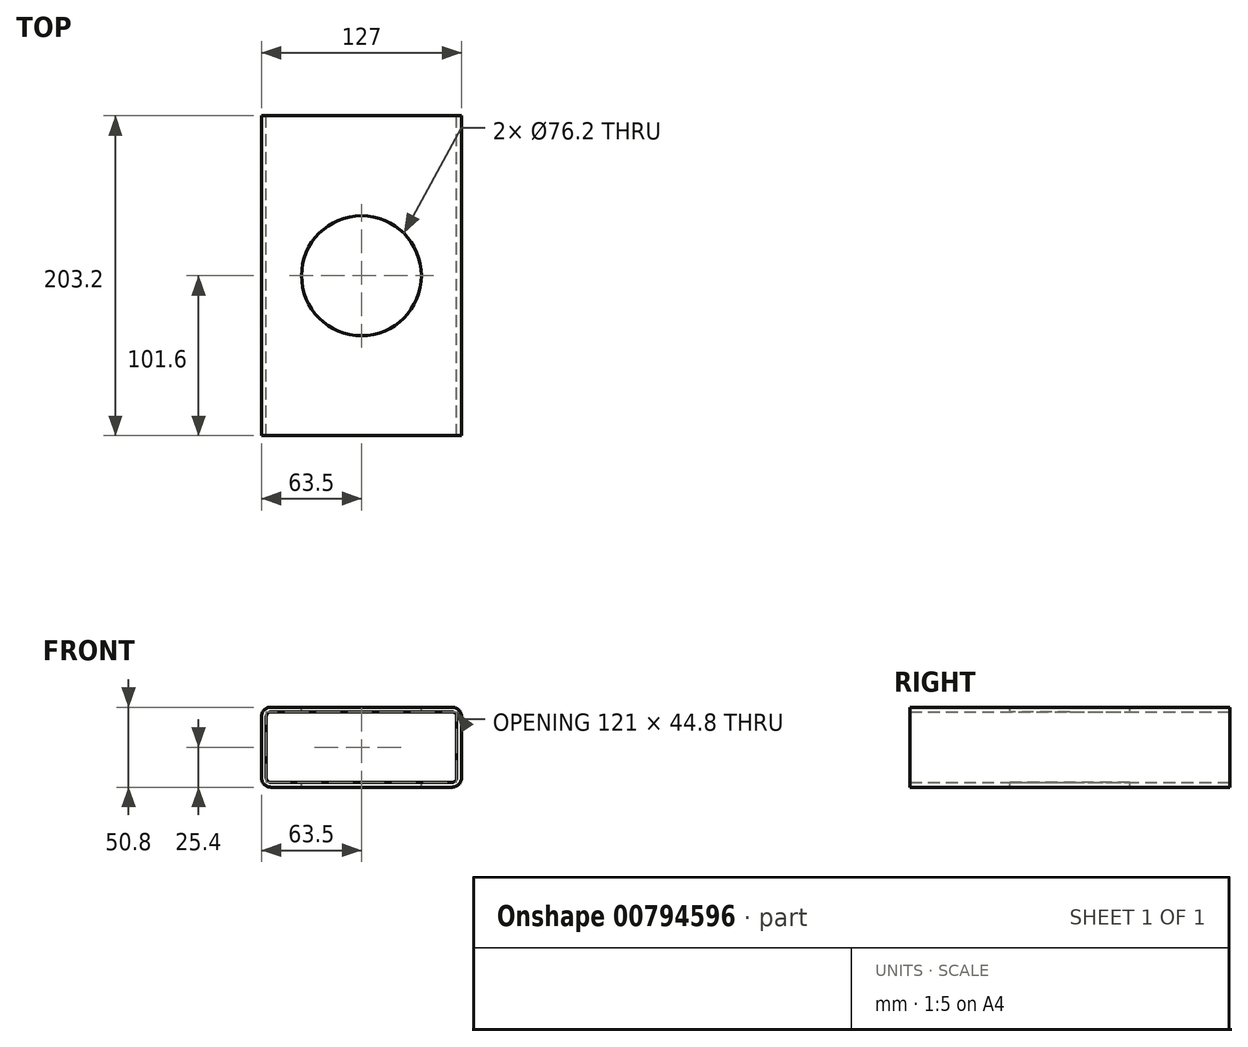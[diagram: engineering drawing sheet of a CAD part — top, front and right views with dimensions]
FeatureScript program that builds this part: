
annotation { "Feature Type Name" : "Feature", "Feature Type Description" : "" }
export const myFeature = defineFeature(function(context is Context, id is Id, definition is map)
    precondition{}
    {
        {
            var Q0;
            Q0=qCreatedBy(makeId("Front.planeOp"),FACE);
            var sketch = newSketch(context, id + "F0", { "sketchPlane" : qUnion([Q0])});
            skLineSegment(sketch, "E0.bottom", {"start": v(57.5, -25.4) * mm, "end": v(-57.5, -25.4) * mm});
            skLineSegment(sketch, "E0.top", {"start": v(57.5, 25.4) * mm, "end": v(-57.5, 25.4) * mm});
            skLineSegment(sketch, "E0.left", {"start": v(63.5, -19.4) * mm, "end": v(63.5, 19.4) * mm});
            skLineSegment(sketch, "E0.right", {"start": v(-63.5, -19.4) * mm, "end": v(-63.5, 19.4) * mm});
            skPoint(sketch, "E0.middle", {"position": v(0, 0) * mm});
            skLineSegment(sketch, "E1.bottom", {"start": v(57.5, -22.4) * mm, "end": v(-57.5, -22.4) * mm});
            skLineSegment(sketch, "E1.top", {"start": v(57.5, 22.4) * mm, "end": v(-57.5, 22.4) * mm});
            skLineSegment(sketch, "E1.left", {"start": v(60.5, -19.4) * mm, "end": v(60.5, 19.4) * mm});
            skLineSegment(sketch, "E1.right", {"start": v(-60.5, -19.4) * mm, "end": v(-60.5, 19.4) * mm});
            skPoint(sketch, "E2.visualSharp", {"position": v(-60.5, 22.4) * mm});
            skArc(sketch, "E2.filletArc", {"start": v(-57.5, 22.4) * mm, "mid": v(-59.62, 21.52) * mm, "end": v(-60.5, 19.4) * mm});
            skPoint(sketch, "E3.visualSharp", {"position": v(-60.5, -22.4) * mm});
            skArc(sketch, "E3.filletArc", {"start": v(-60.5, -19.4) * mm, "mid": v(-59.62, -21.52) * mm, "end": v(-57.5, -22.4) * mm});
            skPoint(sketch, "E4.visualSharp", {"position": v(60.5, -22.4) * mm});
            skArc(sketch, "E4.filletArc", {"start": v(57.5, -22.4) * mm, "mid": v(59.62, -21.52) * mm, "end": v(60.5, -19.4) * mm});
            skPoint(sketch, "E5.visualSharp", {"position": v(60.5, 22.4) * mm});
            skArc(sketch, "E5.filletArc", {"start": v(60.5, 19.4) * mm, "mid": v(59.62, 21.52) * mm, "end": v(57.5, 22.4) * mm});
            skPoint(sketch, "E6.visualSharp", {"position": v(63.5, 25.4) * mm});
            skArc(sketch, "E6.filletArc", {"start": v(63.5, 19.4) * mm, "mid": v(61.74, 23.64) * mm, "end": v(57.5, 25.4) * mm});
            skPoint(sketch, "E7.visualSharp", {"position": v(-63.5, 25.4) * mm});
            skArc(sketch, "E7.filletArc", {"start": v(-57.5, 25.4) * mm, "mid": v(-61.74, 23.64) * mm, "end": v(-63.5, 19.4) * mm});
            skPoint(sketch, "E8.visualSharp", {"position": v(-63.5, -25.4) * mm});
            skArc(sketch, "E8.filletArc", {"start": v(-63.5, -19.4) * mm, "mid": v(-61.74, -23.64) * mm, "end": v(-57.5, -25.4) * mm});
            skPoint(sketch, "E9.visualSharp", {"position": v(63.5, -25.4) * mm});
            skArc(sketch, "E9.filletArc", {"start": v(57.5, -25.4) * mm, "mid": v(61.74, -23.64) * mm, "end": v(63.5, -19.4) * mm});
            skSolve(sketch);
        }
        {
            var Q0;
            Q0 = qSketchRegion(id + "F0", true);
            extrude(context, id + "F1", {"entities" : qUnion([Q0]), "depth" : 203.2 * mm, "offsetDistance" : 25 * mm});
        }
        {
            var Q0;
            Q0=makeQuery(id+"F1.opExtrude","SWEPT_FACE",FACE,{"disambiguationData":[OSD([sQuery(id+"F0.wireOp",EDGE,"E0.top")])]});
            var sketch = newSketch(context, id + "F2", { "sketchPlane" : qUnion([Q0])});
            skCircle(sketch, "E10", {"center": v(0, -101.6) * mm, "radius": 38.1 * mm});
            skSolve(sketch);
        }
        {
            var Q0;
            Q0 = qSketchRegion(id + "F2", true);
            extrude(context, id + "F3", {"entities" : qUnion([Q0]), "operationType" : NewBodyOperationType.REMOVE, "endBound" : BoundingType.THROUGH_ALL, "oppositeDirection" : true, "depth" : 25 * mm, "offsetDistance" : 25 * mm});
        }
    });
